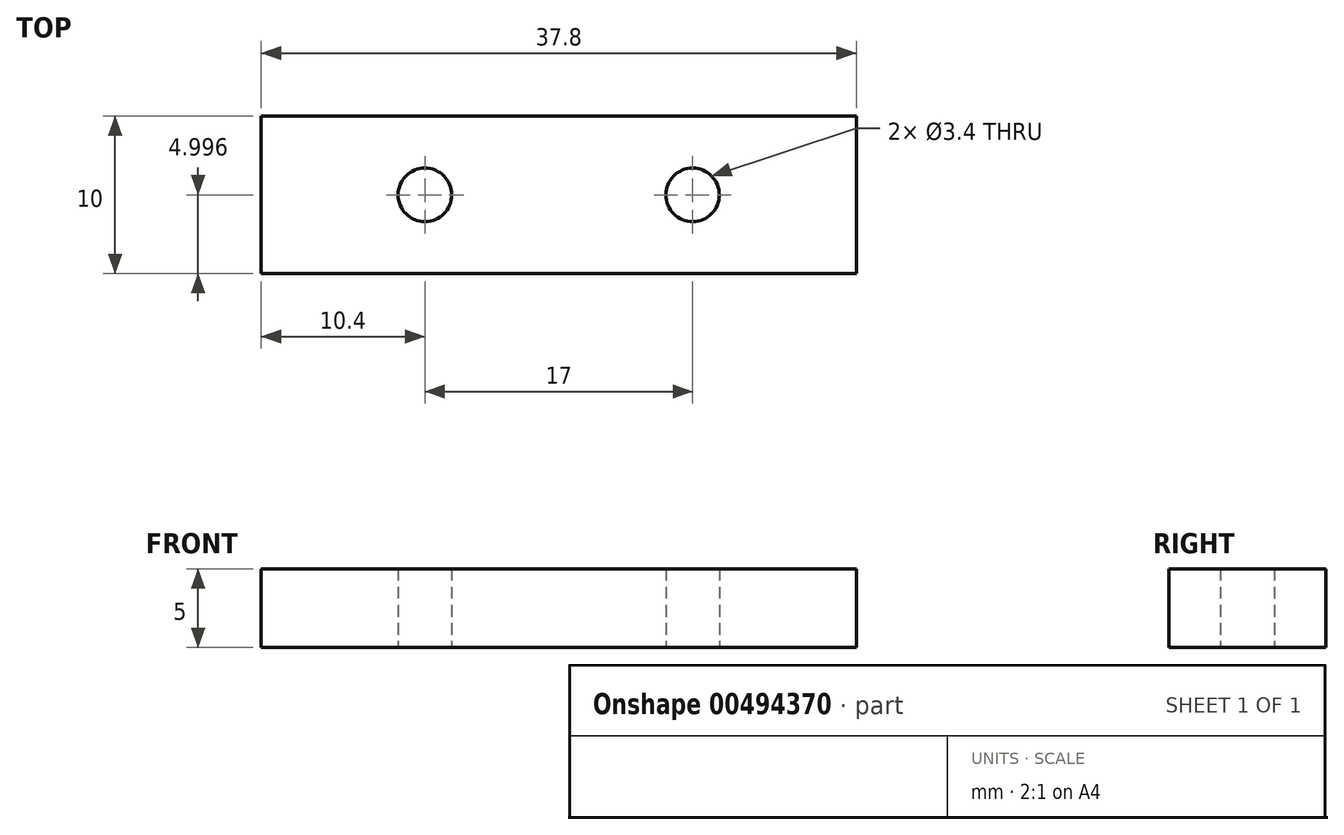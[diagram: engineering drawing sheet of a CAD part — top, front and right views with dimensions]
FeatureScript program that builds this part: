
annotation { "Feature Type Name" : "Feature", "Feature Type Description" : "" }
export const myFeature = defineFeature(function(context is Context, id is Id, definition is map)
    precondition{}
    {
        {
            var Q0;
            Q0=qCreatedBy(makeId("Top.planeOp"),FACE);
            var sketch = newSketch(context, id + "F0", { "sketchPlane" : qUnion([Q0])});
            skLineSegment(sketch, "E0.bottom", {"start": v(-21.75, 22.47) * mm, "end": v(16.05, 22.47) * mm});
            skLineSegment(sketch, "E0.top", {"start": v(-21.75, 12.47) * mm, "end": v(16.05, 12.47) * mm});
            skLineSegment(sketch, "E0.left", {"start": v(-21.75, 22.47) * mm, "end": v(-21.75, 12.47) * mm});
            skLineSegment(sketch, "E0.right", {"start": v(16.05, 22.47) * mm, "end": v(16.05, 12.47) * mm});
            skLineSegment(sketch, "E1", {"start": v(-2.85, 22.47) * mm, "end": v(-2.85, 12.47) * mm});
            skPoint(sketch, "E2", {"position": v(-2.85, 17.47) * mm});
            skCircle(sketch, "E3", {"center": v(-11.35, 17.47) * mm, "radius": 1.7 * mm});
            skCircle(sketch, "E4", {"center": v(5.65, 17.47) * mm, "radius": 1.7 * mm});
            skLineSegment(sketch, "E5", {"start": v(-11.35, 17.47) * mm, "end": v(5.65, 17.47) * mm});
            skSolve(sketch);
        }
        {
            var Q0;
            Q0 = qSketchRegion(id + "F0", true);
            var Q1;
            {var subQ4=sQuery(id+"F0.wireOp",EDGE,"E0.left");Q1=makeQuery(id+"F0.imprint","IMPRINT",FACE,{"disambiguationData":[TD([[makeQuery(id+"F0.imprint","IMPRINT",EDGE,{"derivedFrom":subQ4}),1.0]])]});}
            extrude(context, id + "F1", {"entities" : qUnion([Q0, Q1]), "depth" : 5 * mm});
        }
    });
